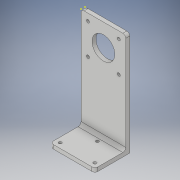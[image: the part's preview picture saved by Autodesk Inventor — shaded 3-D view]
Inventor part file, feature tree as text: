
AUTODESK INVENTOR PART (.ipt)
format: ipt  version: 2017 (Build 210142000, 142)  size: 162,304 bytes
history: native  units: in
note: dims shown in document units (in); Inventor stores cm internally (conversion verified against a paired STEP export)
features: sketch x5, fillet x5, extrude x3
ambient origin geometry x8: Origin, YZ Plane, XZ Plane, XY Plane, X Axis, Y Axis, Z Axis, Center Point
bodies: Solid1 (feature_tree)
feature tree (13):
  sketch  "Sketch1"  dims[d0=1.7717in d1=4.1339in]
  extrude  "Extrusion1"  Depth=4.1339in
  sketch  "Sketch3"  dims[d4=0.1181in d5=0.1181in d6=1.2205in d10=0.2756in d11=0.2756in d12=1.2205in d13=0.2756in]
  extrude  "Extrusion2"  Depth=0.1181in
  extrude  "Extrusion3"  Depth=0.1181in
  fillet  "Fillet1"  Radius=1.2205in
  fillet  "Fillet2"  Radius=0.2756in
  fillet  "Fillet3"  Radius=0.2756in
  fillet  "Fillet4"  Radius=1.2205in
  fillet  "Fillet5"  Radius=0.2756in
  sketch  "Sketch2"  dims[d2=0.1181in d3=0.1181in]
  sketch  "Sketch4"  dims[d14=0.2756in]
  sketch  "Sketch5"  dims[d15=1.2205in d16=1.2205in d17=0.9055in d18=0.8858in d19=0.8858in d20=0.1575in d21=0.0in d22=0.1575in d23=1.2205in d24=0.0in d25=0.1181in d26=0.1181in d27=0.1181in d28=0.1969in d29=0.1969in d30=0.1969in d31=0.1969in d32=0.8858in d33=0.9843in d34=0.1575in d35=0.0in d36=0.1181in d37=0.1181in d38=0.1181in d39=0.1181in d40=0.1181in]
